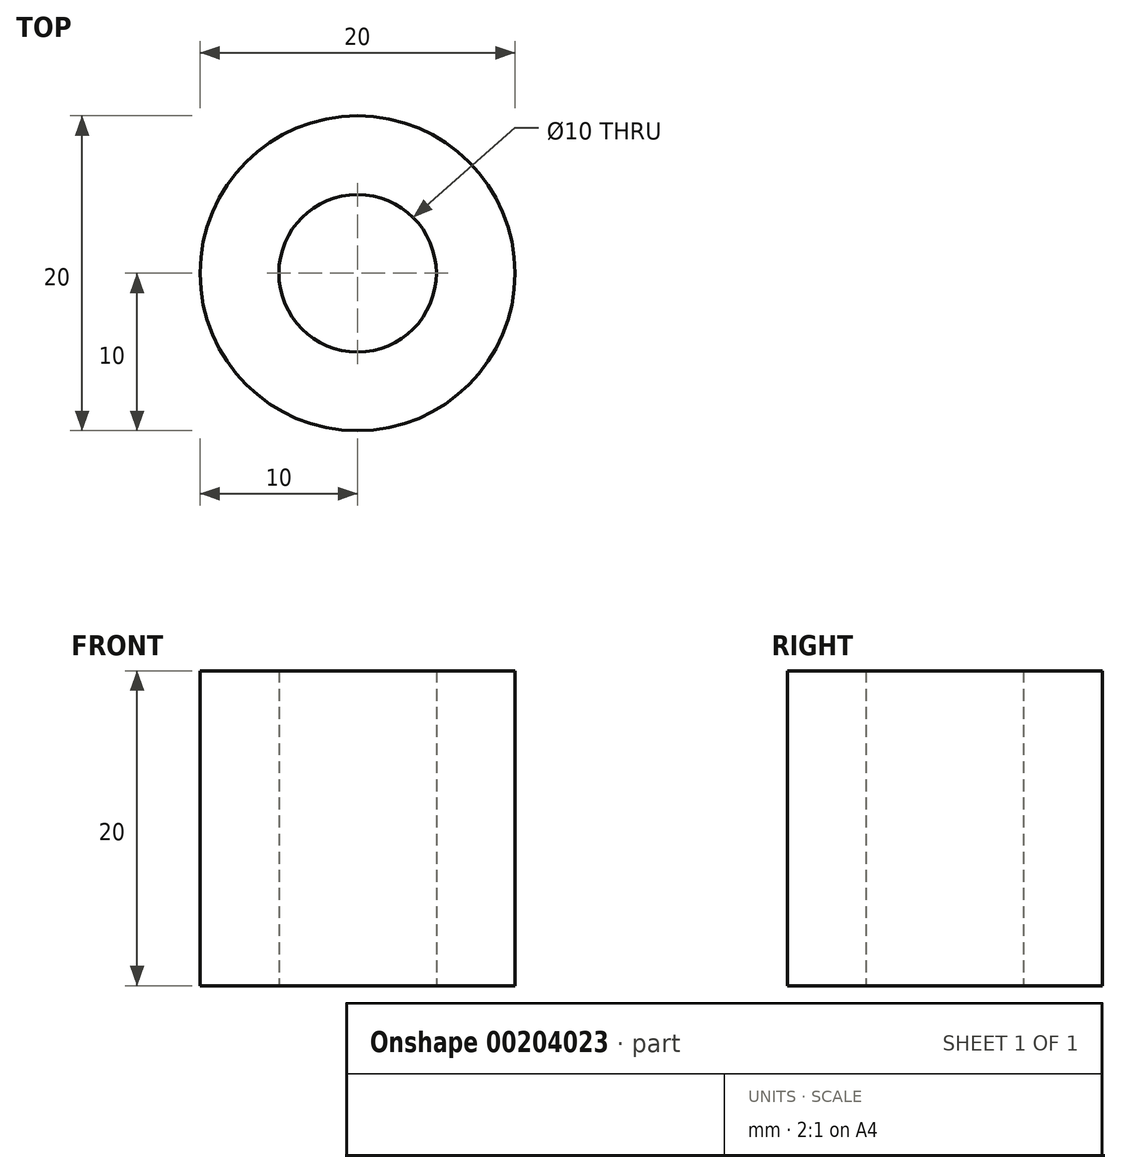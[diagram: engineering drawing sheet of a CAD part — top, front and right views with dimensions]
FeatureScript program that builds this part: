
annotation { "Feature Type Name" : "Feature", "Feature Type Description" : "" }
export const myFeature = defineFeature(function(context is Context, id is Id, definition is map)
    precondition{}
    {
        {
            var Q0;
            Q0=qCreatedBy(makeId("Top.planeOp"),FACE);
            var sketch = newSketch(context, id + "F0", { "sketchPlane" : qUnion([Q0])});
            skCircle(sketch, "E0", {"center": v(0, 0) * mm, "radius": 10 * mm});
            skCircle(sketch, "E1", {"center": v(0, 0) * mm, "radius": 5 * mm});
            skSolve(sketch);
        }
        {
            var Q0;
            Q0=makeQuery(id+"F0.imprint","IMPRINT",FACE,{"disambiguationData":[TD([[makeQuery(id+"F0.imprint","IMPRINT",EDGE,{"derivedFrom":sQuery(id+"F0.wireOp",EDGE,"E0")}),1.0]])]});
            extrude(context, id + "F1", {"entities" : qUnion([Q0]), "depth" : 20 * mm});
        }
    });
